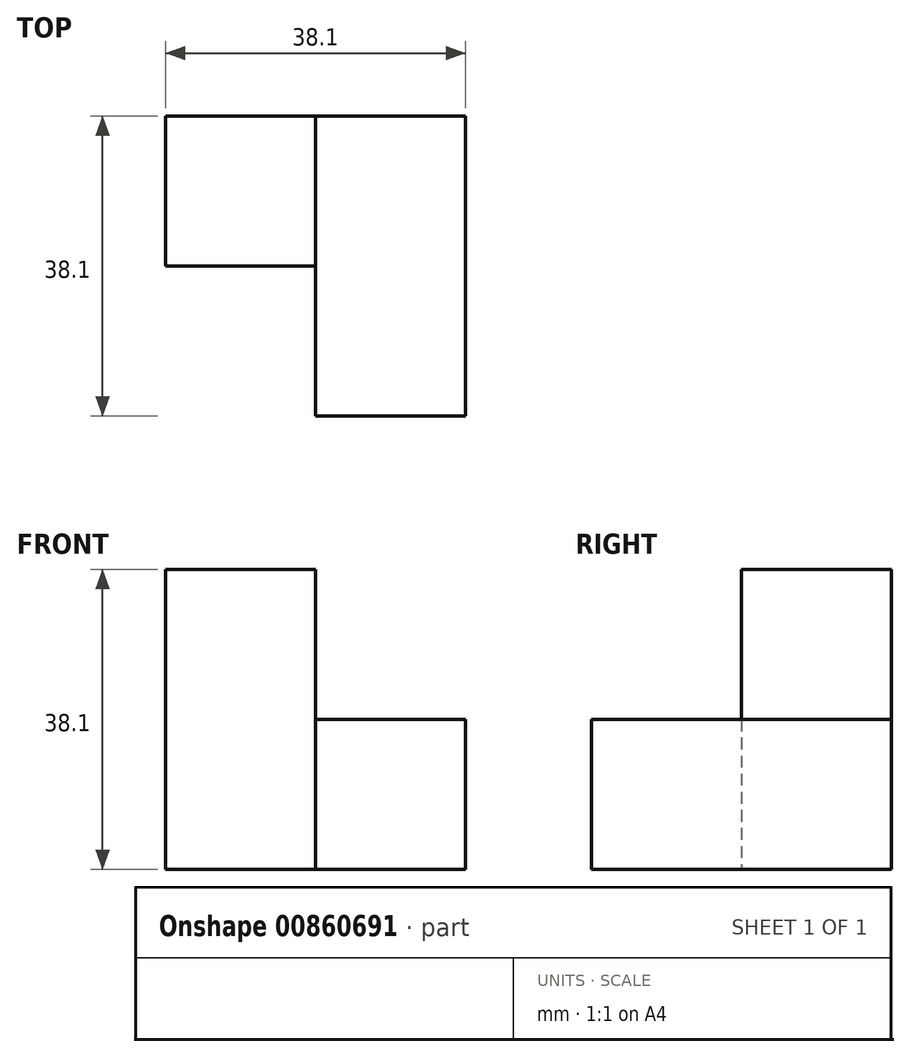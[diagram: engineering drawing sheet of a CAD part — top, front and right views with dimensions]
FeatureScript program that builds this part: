
annotation { "Feature Type Name" : "Feature", "Feature Type Description" : "" }
export const myFeature = defineFeature(function(context is Context, id is Id, definition is map)
    precondition{}
    {
        {
            var Q0;
            Q0=qCreatedBy(makeId("Top.planeOp"),FACE);
            var sketch = newSketch(context, id + "F0", { "sketchPlane" : qUnion([Q0])});
            skLineSegment(sketch, "E0", {"start": v(0, 0) * mm, "end": v(0, 19.05) * mm});
            skLineSegment(sketch, "E1", {"start": v(0, 19.05) * mm, "end": v(38.1, 19.05) * mm});
            skLineSegment(sketch, "E2", {"start": v(38.1, 19.05) * mm, "end": v(38.1, -19.05) * mm});
            skLineSegment(sketch, "E3", {"start": v(38.1, -19.05) * mm, "end": v(19.05, -19.05) * mm});
            skLineSegment(sketch, "E4", {"start": v(19.05, -19.05) * mm, "end": v(19.05, 0) * mm});
            skLineSegment(sketch, "E5", {"start": v(19.05, 0) * mm, "end": v(0, 0) * mm});
            skSolve(sketch);
        }
        {
            var Q0;
            Q0=qSketchRegion(id+"F0",true);
            extrude(context, id + "F1", {"entities" : qUnion([Q0]), "depth" : 19.05 * mm, "offsetDistance" : 25.4 * mm});
        }
        {
            var Q0;
            Q0=makeQuery(id+"F1.opExtrude","CAP_FACE",FACE,{"disambiguationData":[OSD([sQuery(id+"F0.wireOp",EDGE,"E0"),sQuery(id+"F0.wireOp",EDGE,"E1"),sQuery(id+"F0.wireOp",EDGE,"E2"),sQuery(id+"F0.wireOp",EDGE,"E3"),sQuery(id+"F0.wireOp",EDGE,"E4"),sQuery(id+"F0.wireOp",EDGE,"E5")])],"isStart":false});
            var sketch = newSketch(context, id + "F2", { "sketchPlane" : qUnion([Q0])});
            skLineSegment(sketch, "E6", {"start": v(19.05, 0) * mm, "end": v(19.05, 19.05) * mm});
            skLineSegment(sketch, "E7", {"start": v(19.05, 19.05) * mm, "end": v(0, 19.05) * mm});
            skLineSegment(sketch, "E8", {"start": v(0, 19.05) * mm, "end": v(0, 0) * mm});
            skLineSegment(sketch, "E9", {"start": v(0, 0) * mm, "end": v(19.05, 0) * mm});
            skSolve(sketch);
        }
        {
            var Q0;
            Q0=qSketchRegion(id+"F2",true);
            extrude(context, id + "F3", {"entities" : qUnion([Q0]), "operationType" : NewBodyOperationType.ADD, "depth" : 19.05 * mm, "offsetDistance" : 25.4 * mm});
        }
    });
